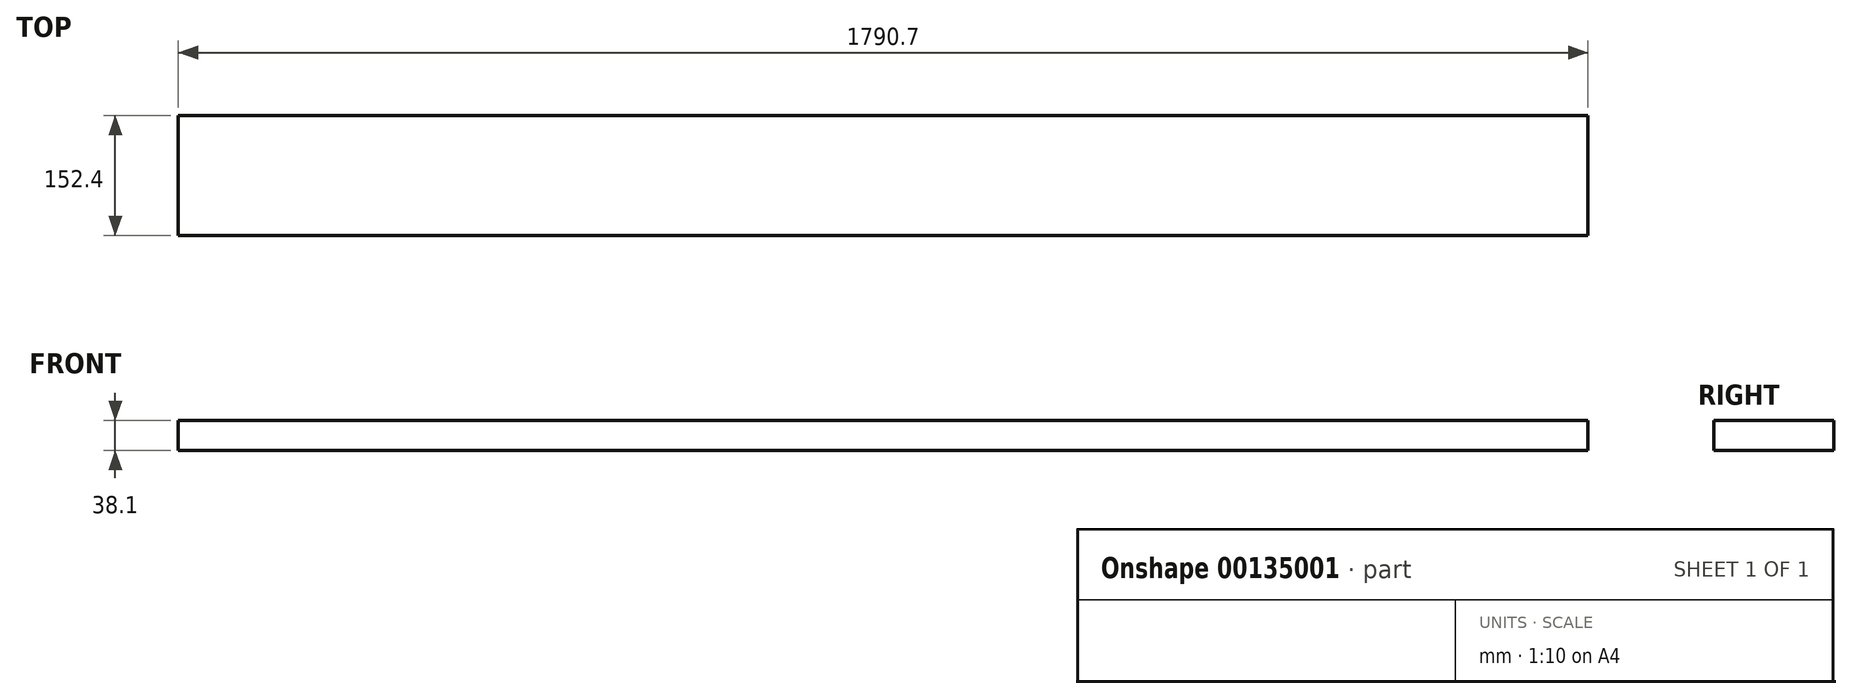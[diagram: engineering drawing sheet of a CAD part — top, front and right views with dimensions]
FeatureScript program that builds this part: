
annotation { "Feature Type Name" : "Feature", "Feature Type Description" : "" }
export const myFeature = defineFeature(function(context is Context, id is Id, definition is map)
    precondition{}
    {
        {
            var Q0;
            Q0=qCreatedBy(makeId("Right.planeOp"),FACE);
            var sketch = newSketch(context, id + "F0", { "sketchPlane" : qUnion([Q0])});
            skLineSegment(sketch, "E0.bottom", {"start": v(0, 0) * mm, "end": v(152.4, 0) * mm});
            skLineSegment(sketch, "E0.top", {"start": v(0, 38.1) * mm, "end": v(152.4, 38.1) * mm});
            skLineSegment(sketch, "E0.left", {"start": v(0, 0) * mm, "end": v(0, 38.1) * mm});
            skLineSegment(sketch, "E0.right", {"start": v(152.4, 0) * mm, "end": v(152.4, 38.1) * mm});
            skSolve(sketch);
        }
        {
            var Q0;
            Q0 = qSketchRegion(id + "F0", true);
            extrude(context, id + "F1", {"entities" : qUnion([Q0]), "depth" : 1790.7 * mm});
        }
    });
